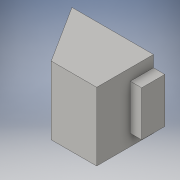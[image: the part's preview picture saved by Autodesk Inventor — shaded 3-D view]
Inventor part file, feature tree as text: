
AUTODESK INVENTOR PART (.ipt)
format: ipt  version: 2016 (Build 200138000, 138)  size: 111,616 bytes
history: native  units: in
note: dims shown in document units (in); Inventor stores cm internally (conversion verified against a paired STEP export)
features: extrude x3, sketch x3
ambient origin geometry x8: Origin, YZ Plane, XZ Plane, XY Plane, X Axis, Y Axis, Z Axis, Center Point
bodies: Solid1 (feature_tree)
feature tree (6):
  extrude  "Extrusion1"  Depth=3.0in
  extrude  "Extrusion2"  Depth=3.0in TaperAngle=0.0deg
  extrude  "Extrusion3"  TaperAngle=90.0deg  [1 undecoded]
  sketch  "Sketch1"  dims[d0=2.0in d1=3.0in]
  sketch  "Sketch2"  dims[d2=2.5in d3=0.0in d5=3.0in d6=0.0in]
  sketch  "Sketch6"  dims[d11=0.991in d12=90.0deg d13=1.9823in d14=1.0209in d15=0.5in d16=0.0in]
note: 1 required parameter value undecoded (feature->parameter linkage not recoverable at this tier; creation-order binding heuristic only, values carry confidence <= 0.55)
